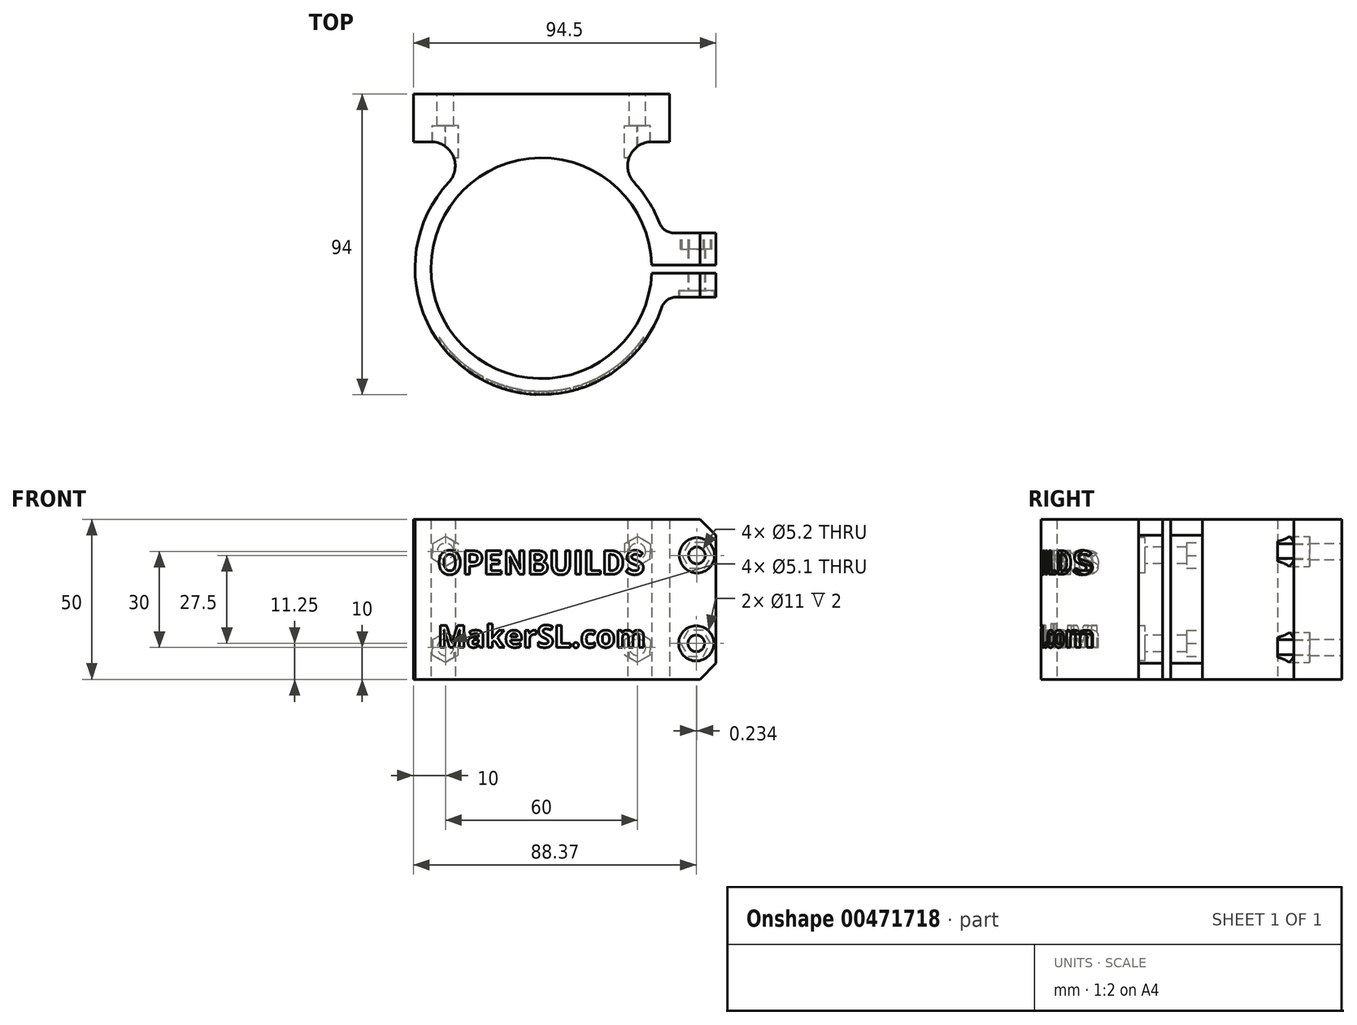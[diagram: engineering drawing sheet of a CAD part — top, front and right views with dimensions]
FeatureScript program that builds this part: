
annotation { "Feature Type Name" : "Feature", "Feature Type Description" : "" }
export const myFeature = defineFeature(function(context is Context, id is Id, definition is map)
    precondition{}
    {
        {
            var Q0;
            Q0=qCreatedBy(makeId("Top.planeOp"),FACE);
            var sketch = newSketch(context, id + "F0", { "sketchPlane" : qUnion([Q0])});
            skArc(sketch, "E0", {"start": v(34.49, 1) * mm, "mid": v(-34.5, 0.25) * mm, "end": v(34.47, -1.5) * mm});
            skArc(sketch, "E1", {"start": v(36.86, 14.2) * mm, "mid": v(33.5, 20.93) * mm, "end": v(28.93, 26.9) * mm});
            skLineSegment(sketch, "E2.bottom", {"start": v(40, 39.5) * mm, "end": v(34.42, 39.5) * mm});
            skLineSegment(sketch, "E2.top", {"start": v(40, 54.5) * mm, "end": v(-40, 54.5) * mm});
            skLineSegment(sketch, "E2.left", {"start": v(40, 39.5) * mm, "end": v(40, 54.5) * mm});
            skLineSegment(sketch, "E2.right", {"start": v(-40, 39.5) * mm, "end": v(-40, 54.5) * mm});
            skPoint(sketch, "E2.middle", {"position": v(0, 47) * mm});
            skLineSegment(sketch, "E3", {"start": v(0, 54.5) * mm, "end": v(0, 34.5) * mm});
            skLineSegment(sketch, "E4.bottom", {"start": v(54.5, -1.5) * mm, "end": v(34.47, -1.5) * mm});
            skLineSegment(sketch, "E4.top", {"start": v(54.5, 1) * mm, "end": v(34.49, 1) * mm});
            skPoint(sketch, "E4.middle", {"position": v(34.5, 0) * mm});
            skLineSegment(sketch, "E5.bottom", {"start": v(54.5, -9) * mm, "end": v(42.24, -9) * mm});
            skLineSegment(sketch, "E5.left", {"start": v(54.5, -9) * mm, "end": v(54.5, -1.5) * mm});
            skLineSegment(sketch, "E6.trimOffspring", {"start": v(54.5, 1) * mm, "end": v(54.5, 8.5) * mm});
            skPoint(sketch, "E7.visualSharp", {"position": v(38.78, 7.5) * mm});
            skPoint(sketch, "E8.visualSharp", {"position": v(38.46, -9) * mm});
            skArc(sketch, "E8.filletArc", {"start": v(42.24, -9) * mm, "mid": v(39.31, -9.95) * mm, "end": v(37.5, -12.43) * mm});
            skArc(sketch, "E9.trimOffspring", {"start": v(-28.93, 26.9) * mm, "mid": v(-20.12, -34) * mm, "end": v(37.5, -12.43) * mm});
            skLineSegment(sketch, "E10.trimOffspring", {"start": v(-34.42, 39.5) * mm, "end": v(-40, 39.5) * mm});
            skArc(sketch, "E11.filletArc", {"start": v(-28.93, 26.9) * mm, "mid": v(-27.55, 35) * mm, "end": v(-34.42, 39.5) * mm});
            skArc(sketch, "E12.filletArc", {"start": v(34.42, 39.5) * mm, "mid": v(27.55, 35) * mm, "end": v(28.93, 26.9) * mm});
            skLineSegment(sketch, "E13.top", {"start": v(54.5, 11) * mm, "end": v(41.52, 11) * mm});
            skLineSegment(sketch, "E13.left", {"start": v(54.5, 8.5) * mm, "end": v(54.5, 11) * mm});
            skPoint(sketch, "E14.visualSharp", {"position": v(37.94, 11) * mm});
            skArc(sketch, "E14.filletArc", {"start": v(36.86, 14.2) * mm, "mid": v(38.7, 11.88) * mm, "end": v(41.52, 11) * mm});
            skSolve(sketch);
        }
        {
            var Q0;
            {var subQ3=sQuery(id+"F0.wireOp",EDGE,"E2.right");Q0=makeQuery(id+"F0.imprint","IMPRINT",FACE,{"disambiguationData":[TD([[makeQuery(id+"F0.imprint","IMPRINT",EDGE,{"derivedFrom":subQ3}),-1.0]])]});}
            var Q1;
            Q1=makeQuery(id+"F0.imprint","IMPRINT",FACE,{"disambiguationData":[TD([[makeQuery(id+"F0.imprint","IMPRINT",EDGE,{"derivedFrom":sQuery(id+"F0.wireOp",EDGE,"E1")}),1.0]])]});
            extrude(context, id + "F1", {"entities" : qUnion([Q0, Q1]), "depth" : 50 * mm});
        }
        {
            var Q0;
            Q0=makeQuery(id+"F1.opExtrude","SWEPT_FACE",FACE,{"disambiguationData":[OSD([sQuery(id+"F0.wireOp",EDGE,"E2.top")])]});
            var sketch = newSketch(context, id + "F2", { "sketchPlane" : qUnion([Q0])});
            skLineSegment(sketch, "E15", {"start": v(-40, 10) * mm, "end": v(40, 10) * mm, "construction": true});
            skLineSegment(sketch, "E16", {"start": v(-40, 40) * mm, "end": v(40, 40) * mm, "construction": true});
            skCircle(sketch, "E17", {"center": v(-30, 10) * mm, "radius": 2.55 * mm});
            skCircle(sketch, "E18", {"center": v(-30, 40) * mm, "radius": 2.55 * mm});
            skCircle(sketch, "E19", {"center": v(30, 40) * mm, "radius": 2.55 * mm});
            skCircle(sketch, "E20", {"center": v(30, 10) * mm, "radius": 2.55 * mm});
            skSolve(sketch);
        }
        {
            var Q0;
            Q0=qSketchRegion(id+"F2",true);
            extrude(context, id + "F3", {"entities" : qUnion([Q0]), "operationType" : NewBodyOperationType.REMOVE, "oppositeDirection" : true, "depth" : 15 * mm});
        }
        {
            var Q0;
            Q0=qCreatedBy(makeId("Front.planeOp"),FACE);
            var sketch = newSketch(context, id + "F4", { "sketchPlane" : qUnion([Q0])});
            skLineSegment(sketch, "E21", {"start": v(0, 25) * mm, "end": v(57.85, 25) * mm});
            skArc(sketch, "E22.0.startCap", {"start": v(0, 22.5) * mm, "mid": v(-2.5, 25) * mm, "end": v(0, 27.5) * mm});
            skArc(sketch, "E22.0.endCap", {"start": v(57.85, 27.5) * mm, "mid": v(60.35, 25) * mm, "end": v(57.85, 22.5) * mm});
            skLineSegment(sketch, "E22.0.left", {"start": v(0, 27.5) * mm, "end": v(57.85, 27.5) * mm});
            skLineSegment(sketch, "E22.0.right", {"start": v(0, 22.5) * mm, "end": v(57.85, 22.5) * mm});
            skSolve(sketch);
        }
        {
            var Q0;
            {var subQ2=sQuery(id+"F0.wireOp",EDGE,"E5.bottom");Q0=makeQuery(id+"FSlxkKbNy0vXjha_1.boolean.opBoolean","SPLIT",FACE,{"disambiguationData":[TD([makeQuery(id+"FSlxkKbNy0vXjha_1.opExtrude","SWEPT_FACE",FACE,{"disambiguationData":[OSD([sQuery(id+"F4.wireOp",EDGE,"E22.0.left")])]})])],"derivedFrom":makeQuery(id+"F1.opExtrude","SWEPT_FACE",FACE,{"disambiguationData":[OSD([subQ2])]})});}
            var sketch = newSketch(context, id + "F5", { "sketchPlane" : qUnion([Q0])});
            skLineSegment(sketch, "E23", {"start": v(48.37, 50) * mm, "end": v(48.37, 0) * mm, "construction": true});
            skLineSegment(sketch, "E24", {"start": v(54.5, 11.25) * mm, "end": v(42.24, 11.25) * mm, "construction": true});
            skCircle(sketch, "E25", {"center": v(48.6, 38.75) * mm, "radius": 2.6 * mm});
            skCircle(sketch, "E26", {"center": v(48.37, 11.25) * mm, "radius": 2.6 * mm});
            skCircle(sketch, "E27", {"center": v(48.6, 38.75) * mm, "radius": 2 * mm});
            skCircle(sketch, "E28", {"center": v(48.37, 11.25) * mm, "radius": 2 * mm});
            skSolve(sketch);
        }
        {
            var Q0;
            Q0=makeQuery(id+"F5.imprint","IMPRINT",FACE,{"disambiguationData":[TD([[makeQuery(id+"F5.imprint","IMPRINT",EDGE,{"derivedFrom":sQuery(id+"F5.wireOp",EDGE,"E26")}),1.0]])]});
            var Q1;
            Q1=makeQuery(id+"F5.imprint","IMPRINT",FACE,{"disambiguationData":[TD([[makeQuery(id+"F5.imprint","IMPRINT",EDGE,{"derivedFrom":sQuery(id+"F5.wireOp",EDGE,"E25")}),1.0]])]});
            var Q2;
            Q2=makeQuery(id+"F5.imprint","IMPRINT",FACE,{"disambiguationData":[TD([[makeQuery(id+"F5.imprint","IMPRINT",EDGE,{"derivedFrom":sQuery(id+"F5.wireOp",EDGE,"E27")}),1.0]])]});
            var Q3;
            Q3=makeQuery(id+"F5.imprint","IMPRINT",FACE,{"disambiguationData":[TD([[makeQuery(id+"F5.imprint","IMPRINT",EDGE,{"derivedFrom":sQuery(id+"F5.wireOp",EDGE,"E28")}),1.0]])]});
            var Q4;
            {var subQ2=sQuery(id+"F0.wireOp",EDGE,"E4.bottom");Q4=makeQuery(id+"FSlxkKbNy0vXjha_1.boolean.opBoolean","SPLIT",FACE,{"disambiguationData":[TD([makeQuery(id+"FSlxkKbNy0vXjha_1.opExtrude","SWEPT_FACE",FACE,{"disambiguationData":[OSD([sQuery(id+"F4.wireOp",EDGE,"E22.0.right")])]})])],"derivedFrom":makeQuery(id+"F1.opExtrude","SWEPT_FACE",FACE,{"disambiguationData":[OSD([subQ2])]})});}
            extrude(context, id + "F6", {"entities" : qUnion([Q0, Q1, Q2, Q3]), "operationType" : NewBodyOperationType.REMOVE, "endBound" : BoundingType.THROUGH_ALL, "oppositeDirection" : true, "endBoundEntityFace" : qUnion([Q4]), "depth" : 25 * mm});
        }
        {
            var Q0;
            Q0=qCreatedBy(makeId("Right.planeOp"),FACE);
            var sketch = newSketch(context, id + "F7", { "sketchPlane" : qUnion([Q0])});
            skLineSegment(sketch, "E29", {"start": v(-2.5, 25) * mm, "end": v(-48.95, 25) * mm});
            skArc(sketch, "E30.0.startCap", {"start": v(-2.5, 27.5) * mm, "mid": v(0, 25) * mm, "end": v(-2.5, 22.5) * mm});
            skArc(sketch, "E30.0.endCap", {"start": v(-48.95, 22.5) * mm, "mid": v(-51.45, 25) * mm, "end": v(-48.95, 27.5) * mm});
            skLineSegment(sketch, "E30.0.left", {"start": v(-2.5, 22.5) * mm, "end": v(-48.95, 22.5) * mm});
            skLineSegment(sketch, "E30.0.right", {"start": v(-2.5, 27.5) * mm, "end": v(-48.95, 27.5) * mm});
            skSolve(sketch);
        }
        {
            var Q0;
            Q0=makeQuery(id+"F1.opExtrude","SWEPT_FACE",FACE,{"disambiguationData":[OSD([sQuery(id+"F0.wireOp",EDGE,"E2.top")])]});
            cPlane(context, id + "F8", {"entities" : qUnion([Q0]), "cplaneType" : CPlaneType.OFFSET, "offset" : 10 * mm, "oppositeDirection" : true, "width" : 150 * mm, "height" : 150 * mm});
        }
        {
            var Q0;
            Q0=qCreatedBy(id+"F8.planeOp",FACE);
            var sketch = newSketch(context, id + "F9", { "sketchPlane" : qUnion([Q0])});
            skCircle(sketch, "E31.cCircle", {"center": v(-30, 10) * mm, "radius": 4.05 * mm, "construction": true});
            skLineSegment(sketch, "E31.0", {"start": v(-26, 12.42) * mm, "end": v(-25.9, 7.75) * mm});
            skLineSegment(sketch, "E31.1", {"start": v(-25.9, 7.75) * mm, "end": v(-29.9, 5.32) * mm});
            skLineSegment(sketch, "E31.2", {"start": v(-29.9, 5.32) * mm, "end": v(-34, 7.58) * mm});
            skLineSegment(sketch, "E31.3", {"start": v(-34, 7.58) * mm, "end": v(-34.1, 12.25) * mm});
            skLineSegment(sketch, "E31.4", {"start": v(-34.1, 12.25) * mm, "end": v(-30.1, 14.68) * mm});
            skLineSegment(sketch, "E31.5", {"start": v(-30.1, 14.68) * mm, "end": v(-26, 12.42) * mm});
            skPoint(sketch, "E31.0.midPoint", {"position": v(-25.95, 10.09) * mm});
            skCircle(sketch, "E32.0.1.0", {"center": v(-30, 40) * mm, "radius": 4.05 * mm, "construction": true});
            skLineSegment(sketch, "E32.0.1.1", {"start": v(-25.9, 37.75) * mm, "end": v(-29.9, 35.32) * mm});
            skLineSegment(sketch, "E32.0.1.2", {"start": v(-30.1, 44.68) * mm, "end": v(-26, 42.42) * mm});
            skPoint(sketch, "E32.0.1.3", {"position": v(-25.95, 40.09) * mm});
            skLineSegment(sketch, "E32.0.1.4", {"start": v(-29.9, 35.32) * mm, "end": v(-34, 37.58) * mm});
            skLineSegment(sketch, "E32.0.1.5", {"start": v(-34.1, 42.25) * mm, "end": v(-30.1, 44.68) * mm});
            skLineSegment(sketch, "E32.0.1.6", {"start": v(-26, 42.42) * mm, "end": v(-25.9, 37.75) * mm});
            skLineSegment(sketch, "E32.0.1.7", {"start": v(-34, 37.58) * mm, "end": v(-34.1, 42.25) * mm});
            skCircle(sketch, "E32.1.0.0", {"center": v(30, 10) * mm, "radius": 4.05 * mm, "construction": true});
            skLineSegment(sketch, "E32.1.0.1", {"start": v(34.1, 7.75) * mm, "end": v(30.1, 5.32) * mm});
            skLineSegment(sketch, "E32.1.0.2", {"start": v(29.9, 14.68) * mm, "end": v(34, 12.42) * mm});
            skPoint(sketch, "E32.1.0.3", {"position": v(34.05, 10.09) * mm});
            skLineSegment(sketch, "E32.1.0.4", {"start": v(30.1, 5.32) * mm, "end": v(26, 7.58) * mm});
            skLineSegment(sketch, "E32.1.0.5", {"start": v(25.9, 12.25) * mm, "end": v(29.9, 14.68) * mm});
            skLineSegment(sketch, "E32.1.0.6", {"start": v(34, 12.42) * mm, "end": v(34.1, 7.75) * mm});
            skLineSegment(sketch, "E32.1.0.7", {"start": v(26, 7.58) * mm, "end": v(25.9, 12.25) * mm});
            skCircle(sketch, "E32.1.1.0", {"center": v(30, 40) * mm, "radius": 4.05 * mm, "construction": true});
            skLineSegment(sketch, "E32.1.1.1", {"start": v(34.1, 37.75) * mm, "end": v(30.1, 35.32) * mm});
            skLineSegment(sketch, "E32.1.1.2", {"start": v(29.9, 44.68) * mm, "end": v(34, 42.42) * mm});
            skPoint(sketch, "E32.1.1.3", {"position": v(34.05, 40.09) * mm});
            skLineSegment(sketch, "E32.1.1.4", {"start": v(30.1, 35.32) * mm, "end": v(26, 37.58) * mm});
            skLineSegment(sketch, "E32.1.1.5", {"start": v(25.9, 42.25) * mm, "end": v(29.9, 44.68) * mm});
            skLineSegment(sketch, "E32.1.1.6", {"start": v(34, 42.42) * mm, "end": v(34.1, 37.75) * mm});
            skLineSegment(sketch, "E32.1.1.7", {"start": v(26, 37.58) * mm, "end": v(25.9, 42.25) * mm});
            skLineSegment(sketch, "E32.direction1", {"start": v(-34, 7.58) * mm, "end": v(26, 7.58) * mm, "construction": true});
            skLineSegment(sketch, "E32.direction2", {"start": v(-34, 7.58) * mm, "end": v(-34, 37.58) * mm, "construction": true});
            skSolve(sketch);
        }
        {
            var Q0;
            Q0=qSketchRegion(id+"F9",true);
            extrude(context, id + "F10", {"entities" : qUnion([Q0]), "operationType" : NewBodyOperationType.REMOVE, "oppositeDirection" : true, "depth" : 10 * mm});
        }
        {
            var Q0;
            Q0=makeQuery(id+"F1.opExtrude","SWEPT_FACE",FACE,{"disambiguationData":[OSD([sQuery(id+"F0.wireOp",EDGE,"E13.top")])]});
            var sketch = newSketch(context, id + "F11", { "sketchPlane" : qUnion([Q0])});
            skCircle(sketch, "E33.cCircle", {"center": v(-48.6, 38.75) * mm, "radius": 4.05 * mm, "construction": true});
            skLineSegment(sketch, "E33.0", {"start": v(-43.93, 38.75) * mm, "end": v(-46.27, 34.7) * mm});
            skLineSegment(sketch, "E33.1", {"start": v(-46.27, 34.7) * mm, "end": v(-50.94, 34.7) * mm});
            skLineSegment(sketch, "E33.2", {"start": v(-50.94, 34.7) * mm, "end": v(-53.28, 38.75) * mm});
            skLineSegment(sketch, "E33.3", {"start": v(-53.28, 38.75) * mm, "end": v(-50.94, 42.8) * mm});
            skLineSegment(sketch, "E33.4", {"start": v(-50.94, 42.8) * mm, "end": v(-46.27, 42.8) * mm});
            skLineSegment(sketch, "E33.5", {"start": v(-46.27, 42.8) * mm, "end": v(-43.93, 38.75) * mm});
            skPoint(sketch, "E33.0.midPoint", {"position": v(-45.1, 36.73) * mm});
            skCircle(sketch, "E34.cCircle", {"center": v(-48.2, 11.25) * mm, "radius": 4.05 * mm, "construction": true});
            skLineSegment(sketch, "E34.0", {"start": v(-43.52, 11.25) * mm, "end": v(-45.86, 7.2) * mm});
            skLineSegment(sketch, "E34.1", {"start": v(-45.86, 7.2) * mm, "end": v(-50.54, 7.2) * mm});
            skLineSegment(sketch, "E34.2", {"start": v(-50.54, 7.2) * mm, "end": v(-52.87, 11.25) * mm});
            skLineSegment(sketch, "E34.3", {"start": v(-52.87, 11.25) * mm, "end": v(-50.54, 15.3) * mm});
            skLineSegment(sketch, "E34.4", {"start": v(-50.54, 15.3) * mm, "end": v(-45.86, 15.3) * mm});
            skLineSegment(sketch, "E34.5", {"start": v(-45.86, 15.3) * mm, "end": v(-43.52, 11.25) * mm});
            skPoint(sketch, "E34.0.midPoint", {"position": v(-44.7, 9.22) * mm});
            skSolve(sketch);
        }
        {
            var Q0;
            Q0=qSketchRegion(id+"F11",true);
            extrude(context, id + "F12", {"entities" : qUnion([Q0]), "operationType" : NewBodyOperationType.REMOVE, "oppositeDirection" : true, "depth" : 5 * mm});
        }
        {
            var Q0;
            Q0=qCreatedBy(makeId("Front.planeOp"),FACE);
            cPlane(context, id + "F13", {"entities" : qUnion([Q0]), "cplaneType" : CPlaneType.OFFSET, "offset" : 50 * mm, "width" : 150 * mm, "height" : 150 * mm});
        }
        {
            var Q0;
            Q0=qCreatedBy(id+"F13.planeOp",FACE);
            var sketch = newSketch(context, id + "F14", { "sketchPlane" : qUnion([Q0])});
            skText(sketch, "E35", { "text": "OPENBUILDS", "fontName": "NotoSansCJKsc-Bold.otf"});
            skText(sketch, "E36", { "text": "MakerSL.com", "fontName": "OpenSans-Bold.ttf"});
            const initialGuessF14  = {"E35": [-0.0325, 0.0328, 1, 0, 0.0072], "E36": [-0.0325, 0.01, 1, 0, 0.00697]};
            skSetInitialGuess(sketch, initialGuessF14);
            skSolve(sketch);
        }
        {
            var Q0;
            Q0=qSketchRegion(id+"F14",true);
            extrude(context, id + "F15", {"entities" : qUnion([Q0]), "operationType" : NewBodyOperationType.REMOVE, "oppositeDirection" : true, "depth" : 50 * mm});
        }
        {
            var Q0;
            Q0=makeQuery(id+"F1.opExtrude","CAP_FACE",FACE,{"disambiguationData":[OSD([sQuery(id+"F0.wireOp",EDGE,"E0"),sQuery(id+"F0.wireOp",EDGE,"E1"),sQuery(id+"F0.wireOp",EDGE,"E2.bottom"),sQuery(id+"F0.wireOp",EDGE,"E2.top"),sQuery(id+"F0.wireOp",EDGE,"E2.left"),sQuery(id+"F0.wireOp",EDGE,"E2.right"),sQuery(id+"F0.wireOp",EDGE,"E4.bottom"),sQuery(id+"F0.wireOp",EDGE,"E4.top"),sQuery(id+"F0.wireOp",EDGE,"E5.bottom"),sQuery(id+"F0.wireOp",EDGE,"E5.left"),sQuery(id+"F0.wireOp",EDGE,"E6.trimOffspring"),sQuery(id+"F0.wireOp",EDGE,"E8.filletArc"),sQuery(id+"F0.wireOp",EDGE,"E9.trimOffspring"),sQuery(id+"F0.wireOp",EDGE,"E10.trimOffspring"),sQuery(id+"F0.wireOp",EDGE,"E11.filletArc"),sQuery(id+"F0.wireOp",EDGE,"E12.filletArc"),sQuery(id+"F0.wireOp",EDGE,"E13.top"),sQuery(id+"F0.wireOp",EDGE,"E13.left"),sQuery(id+"F0.wireOp",EDGE,"E14.filletArc")])],"isStart":false});
            var sketch = newSketch(context, id + "F16", { "sketchPlane" : qUnion([Q0])});
            skArc(sketch, "E37", {"start": v(-34.5, 0) * mm, "mid": v(-2.28, -34.42) * mm, "end": v(34.2, -4.54) * mm});
            skArc(sketch, "E38", {"start": v(-38.5, 0) * mm, "mid": v(-2.54, -38.42) * mm, "end": v(38.16, -5.07) * mm});
            skLineSegment(sketch, "E39", {"start": v(-34.5, 0) * mm, "end": v(-38.5, 0) * mm});
            skLineSegment(sketch, "E40", {"start": v(34.2, -4.54) * mm, "end": v(38.16, -5.07) * mm});
            skSolve(sketch);
        }
        {
            var Q0;
            Q0=makeQuery(id+"F16.imprint","IMPRINT",FACE,{"disambiguationData":[TD([[makeQuery(id+"F16.imprint","IMPRINT",EDGE,{"derivedFrom":sQuery(id+"F16.wireOp",EDGE,"E37")}),-1.0]])]});
            extrude(context, id + "F17", {"entities" : qUnion([Q0]), "operationType" : NewBodyOperationType.ADD, "oppositeDirection" : true, "depth" : 49 * mm});
        }
        {
            var Q0;
            Q0=makeQuery(id+"F1.opExtrude","CAP_EDGE",EDGE,{"disambiguationData":[OSD([sQuery(id+"F0.wireOp",EDGE,"E5.left")])],"isStart":false});
            var Q1;
            Q1=makeQuery(id+"F1.opExtrude","CAP_EDGE",EDGE,{"disambiguationData":[OSD([sQuery(id+"F0.wireOp",EDGE,"E6.trimOffspring"),sQuery(id+"F0.wireOp",EDGE,"E13.left")])],"isStart":false});
            var Q2;
            Q2=makeQuery(id+"F1.opExtrude","CAP_EDGE",EDGE,{"disambiguationData":[OSD([sQuery(id+"F0.wireOp",EDGE,"E6.trimOffspring"),sQuery(id+"F0.wireOp",EDGE,"E13.left")])],"isStart":true});
            var Q3;
            Q3=makeQuery(id+"F1.opExtrude","CAP_EDGE",EDGE,{"disambiguationData":[OSD([sQuery(id+"F0.wireOp",EDGE,"E5.left")])],"isStart":true});
            chamfer(context, id + "F18", {"entities" : qUnion([Q0, Q1, Q2, Q3]), "width" : 5 * mm, "tangentPropagation" : true});
        }
        {
            var Q0;
            Q0=qCreatedBy(makeId("Right.planeOp"),FACE);
            cPlane(context, id + "F19", {"entities" : qUnion([Q0]), "cplaneType" : CPlaneType.OFFSET, "offset" : 50 * mm, "oppositeDirection" : true, "width" : 150 * mm, "height" : 150 * mm});
        }
        {
            var Q0;
            Q0=makeQuery(id+"F1.opExtrude","SWEPT_FACE",FACE,{"disambiguationData":[OSD([sQuery(id+"F0.wireOp",EDGE,"E5.bottom")])]});
            var sketch = newSketch(context, id + "F20", { "sketchPlane" : qUnion([Q0])});
            skCircle(sketch, "E41", {"center": v(48.6, 38.75) * mm, "radius": 5.5 * mm});
            skCircle(sketch, "E42", {"center": v(48.37, 11.25) * mm, "radius": 5.5 * mm});
            skSolve(sketch);
        }
        {
            var Q0;
            Q0=makeQuery(id+"F20.imprint","IMPRINT",FACE,{"disambiguationData":[TD([[makeQuery(id+"F20.imprint","IMPRINT",EDGE,{"derivedFrom":sQuery(id+"F20.wireOp",EDGE,"E41")}),1.0]])]});
            var Q1;
            Q1=makeQuery(id+"F20.imprint","IMPRINT",FACE,{"disambiguationData":[TD([[makeQuery(id+"F20.imprint","IMPRINT",EDGE,{"derivedFrom":sQuery(id+"F20.wireOp",EDGE,"E42")}),1.0]])]});
            extrude(context, id + "F21", {"entities" : qUnion([Q0, Q1]), "operationType" : NewBodyOperationType.REMOVE, "oppositeDirection" : true, "depth" : 2 * mm});
        }
    });
